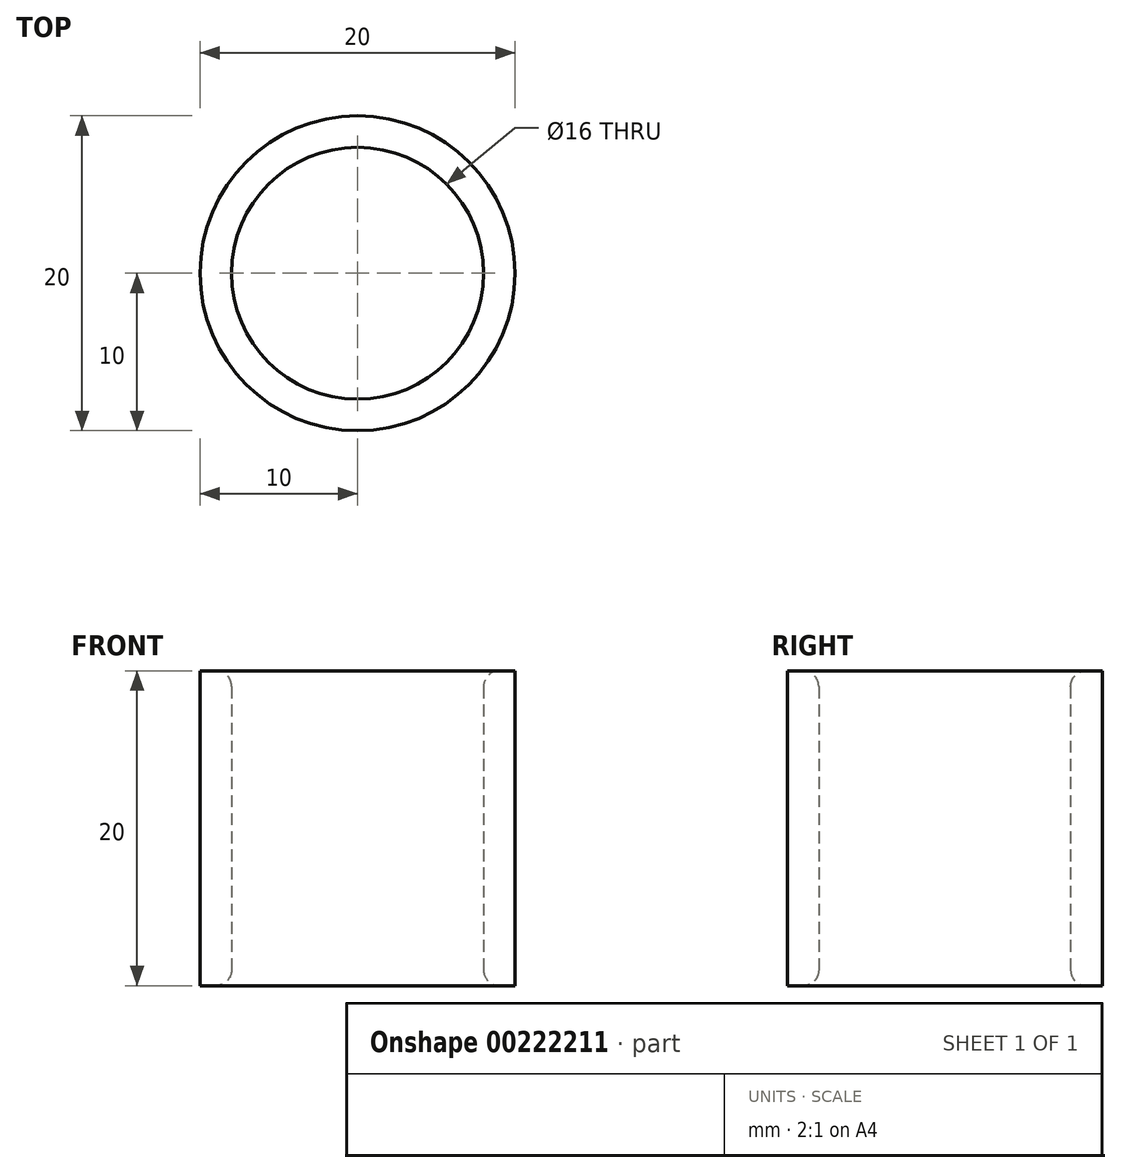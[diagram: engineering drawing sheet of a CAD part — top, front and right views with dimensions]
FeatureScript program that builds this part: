
annotation { "Feature Type Name" : "Feature", "Feature Type Description" : "" }
export const myFeature = defineFeature(function(context is Context, id is Id, definition is map)
    precondition{}
    {
        {
            assignVariable(context, id + "F0", {"name" : "thick", "anyValue" : 2});
        }
        {
            assignVariable(context, id + "F1", {"name" : "size", "anyValue" : 20});
        }
        {
            var Q0;
            Q0=qCreatedBy(makeId("Top.planeOp"),FACE);
            var sketch = newSketch(context, id + "F2", { "sketchPlane" : qUnion([Q0])});
            skCircle(sketch, "E0", {"center": v(0, 0) * mm, "radius": 8 * mm});
            skCircle(sketch, "E1", {"center": v(0, 0) * mm, "radius": 10 * mm});
            skSolve(sketch);
        }
        {
            var Q0;
            Q0=makeQuery(id+"F2.imprint","IMPRINT",FACE,{"disambiguationData":[TD([[makeQuery(id+"F2.imprint","IMPRINT",EDGE,{"derivedFrom":sQuery(id+"F2.wireOp",EDGE,"E0")}),-1.0]])]});
            extrude(context, id + "F3", {"entities" : qUnion([Q0]), "depth" : (getVariable(context, 'size')) * mm});
        }
        {
            var Q0;
            Q0=makeQuery(id+"F3.opExtrude","CAP_EDGE",EDGE,{"disambiguationData":[OSD([sQuery(id+"F2.wireOp",EDGE,"E0")])],"isStart":false});
            fillet(context, id + "F4", {"entities" : qUnion([Q0]), "radius" : (getVariable(context, 'thick') / 2) * mm, "tangentPropagation" : true, "allowEdgeOverflow" : false});
        }
        {
            var Q0;
            Q0=makeQuery(id+"F3.opExtrude","CAP_EDGE",EDGE,{"disambiguationData":[OSD([sQuery(id+"F2.wireOp",EDGE,"E0")])],"isStart":true});
            fillet(context, id + "F5", {"entities" : qUnion([Q0]), "radius" : (getVariable(context, 'thick') / 2) * mm, "tangentPropagation" : true, "allowEdgeOverflow" : false});
        }
    });
